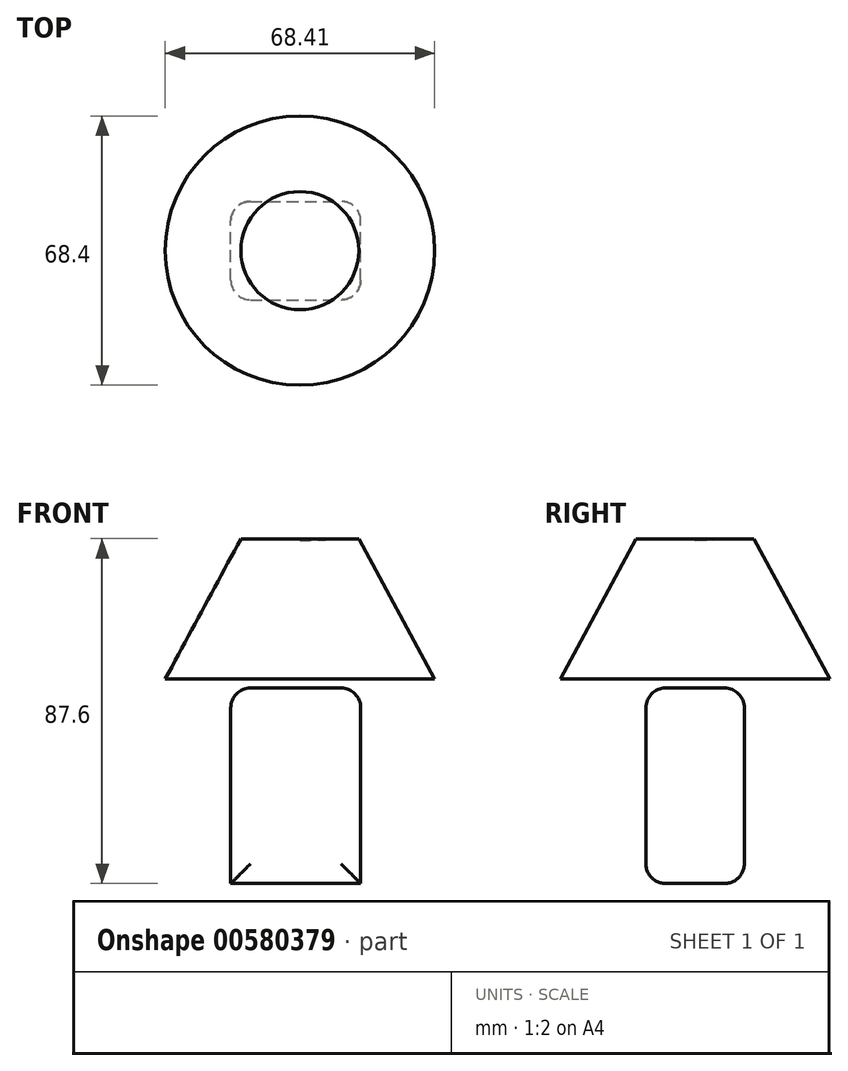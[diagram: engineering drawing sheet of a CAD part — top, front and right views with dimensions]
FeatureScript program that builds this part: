
annotation { "Feature Type Name" : "Feature", "Feature Type Description" : "" }
export const myFeature = defineFeature(function(context is Context, id is Id, definition is map)
    precondition{}
    {
        {
            var Q0;
            Q0=qCreatedBy(makeId("Front.planeOp"),FACE);
            var sketch = newSketch(context, id + "F0", { "sketchPlane" : qUnion([Q0])});
            skLineSegment(sketch, "E0", {"start": v(10.24, 7.64) * mm, "end": v(44.45, 7.64) * mm});
            skLineSegment(sketch, "E1", {"start": v(44.45, 7.64) * mm, "end": v(25.24, 43.25) * mm});
            skLineSegment(sketch, "E2", {"start": v(10.24, 7.64) * mm, "end": v(10.24, 42.78) * mm});
            skLineSegment(sketch, "E3", {"start": v(10.24, 42.78) * mm, "end": v(25.24, 43.25) * mm});
            skSolve(sketch);
        }
        {
            var Q0;
            Q0=makeQuery(id+"F0.imprint","IMPRINT",FACE,{"disambiguationData":[TD([[makeQuery(id+"F0.imprint","IMPRINT",EDGE,{"derivedFrom":sQuery(id+"F0.wireOp",EDGE,"E0")}),1.0]])]});
            var Q1;
            Q1=sQuery(id+"F0.wireOp",EDGE,"E2");
            revolve(context, id + "F1", {"entities" : qUnion([Q0]), "axis" : qUnion([Q1]), "revolveType" : RevolveType.FULL});
        }
        {
            var Q0;
            Q0=qCreatedBy(makeId("Front.planeOp"),FACE);
            var sketch = newSketch(context, id + "F2", { "sketchPlane" : qUnion([Q0])});
            skLineSegment(sketch, "E4.bottom", {"start": v(-7.31, 5.3) * mm, "end": v(25.7, 5.3) * mm});
            skLineSegment(sketch, "E4.top", {"start": v(-7.31, -44.35) * mm, "end": v(25.7, -44.35) * mm});
            skLineSegment(sketch, "E4.left", {"start": v(-7.31, 5.3) * mm, "end": v(-7.31, -44.35) * mm});
            skLineSegment(sketch, "E4.right", {"start": v(25.7, 5.3) * mm, "end": v(25.7, -44.35) * mm});
            skSolve(sketch);
        }
        {
            var Q0;
            Q0 = qSketchRegion(id + "F2", true);
            var Q1;
            Q1=makeQuery(id+"F2.imprint","IMPRINT",FACE,{"disambiguationData":[TD([[makeQuery(id+"F2.imprint","IMPRINT",EDGE,{"derivedFrom":sQuery(id+"F2.wireOp",EDGE,"E4.bottom")}),-1.0]])]});
            extrude(context, id + "F3", {"entities" : qUnion([Q0, Q1]), "endBound" : BoundingType.SYMMETRIC, "depth" : 25 * mm, "offsetDistance" : 25 * mm});
        }
        {
            var Q0;
            Q0=makeQuery(id+"F3.opExtrude","CAP_EDGE",EDGE,{"disambiguationData":[OSD([sQuery(id+"F2.wireOp",EDGE,"E4.bottom")])],"isStart":true});
            fillet(context, id + "F4", {"entities" : qUnion([Q0]), "radius" : 5 * mm, "tangentPropagation" : true, "allowEdgeOverflow" : false});
        }
        {
            var Q0;
            Q0=makeQuery(id+"F3.opExtrude","CAP_FACE",FACE,{"disambiguationData":[OSD([sQuery(id+"F2.wireOp",EDGE,"E4.bottom"),sQuery(id+"F2.wireOp",EDGE,"E4.top"),sQuery(id+"F2.wireOp",EDGE,"E4.left"),sQuery(id+"F2.wireOp",EDGE,"E4.right")])],"isStart":false});
            fillet(context, id + "F5", {"entities" : qUnion([Q0]), "radius" : 5 * mm, "tangentPropagation" : true, "allowEdgeOverflow" : false});
        }
        {
            var Q0;
            Q0=makeQuery(id+"F3.opExtrude","CAP_FACE",FACE,{"disambiguationData":[OSD([sQuery(id+"F2.wireOp",EDGE,"E4.bottom"),sQuery(id+"F2.wireOp",EDGE,"E4.top"),sQuery(id+"F2.wireOp",EDGE,"E4.left"),sQuery(id+"F2.wireOp",EDGE,"E4.right")])],"isStart":true});
            fillet(context, id + "F6", {"entities" : qUnion([Q0]), "radius" : 5 * mm, "tangentPropagation" : true, "allowEdgeOverflow" : false});
        }
    });
